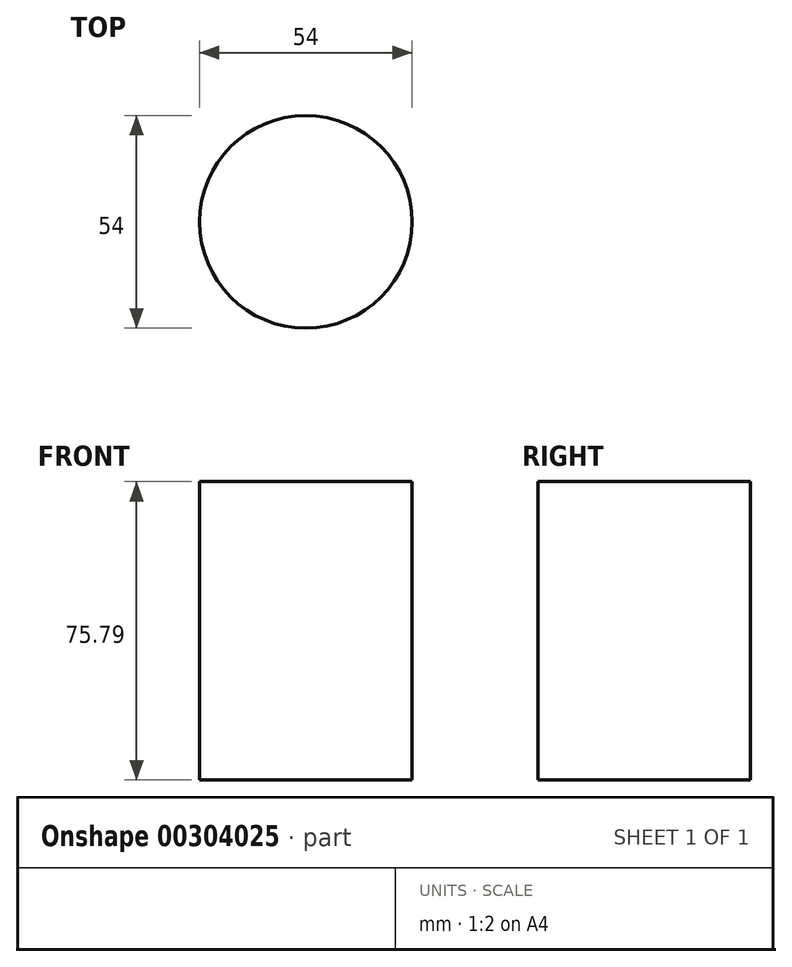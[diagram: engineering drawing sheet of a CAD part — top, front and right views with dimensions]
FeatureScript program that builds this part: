
annotation { "Feature Type Name" : "Feature", "Feature Type Description" : "" }
export const myFeature = defineFeature(function(context is Context, id is Id, definition is map)
    precondition{}
    {
        {
            var Q0;
            Q0=qCreatedBy(makeId("Front.planeOp"),FACE);
            var sketch = newSketch(context, id + "F0", { "sketchPlane" : qUnion([Q0])});
            skLineSegment(sketch, "E0.bottom", {"start": v(-11.84, 36.36) * mm, "end": v(15.16, 36.36) * mm});
            skLineSegment(sketch, "E0.top", {"start": v(-11.84, -39.43) * mm, "end": v(15.16, -39.43) * mm});
            skLineSegment(sketch, "E0.left", {"start": v(-11.84, 36.36) * mm, "end": v(-11.84, -39.43) * mm});
            skLineSegment(sketch, "E0.right", {"start": v(15.16, 36.36) * mm, "end": v(15.16, -39.43) * mm});
            skSolve(sketch);
        }
        {
            var Q0;
            Q0=makeQuery(id+"F0.imprint","IMPRINT",FACE,{"disambiguationData":[TD([[makeQuery(id+"F0.imprint","IMPRINT",EDGE,{"derivedFrom":sQuery(id+"F0.wireOp",EDGE,"E0.bottom")}),-1.0]])]});
            var Q1;
            Q1=sQuery(id+"F0.wireOp",EDGE,"E0.left");
            revolve(context, id + "F1", {"entities" : qUnion([Q0]), "axis" : qUnion([Q1]), "revolveType" : RevolveType.FULL});
        }
    });
